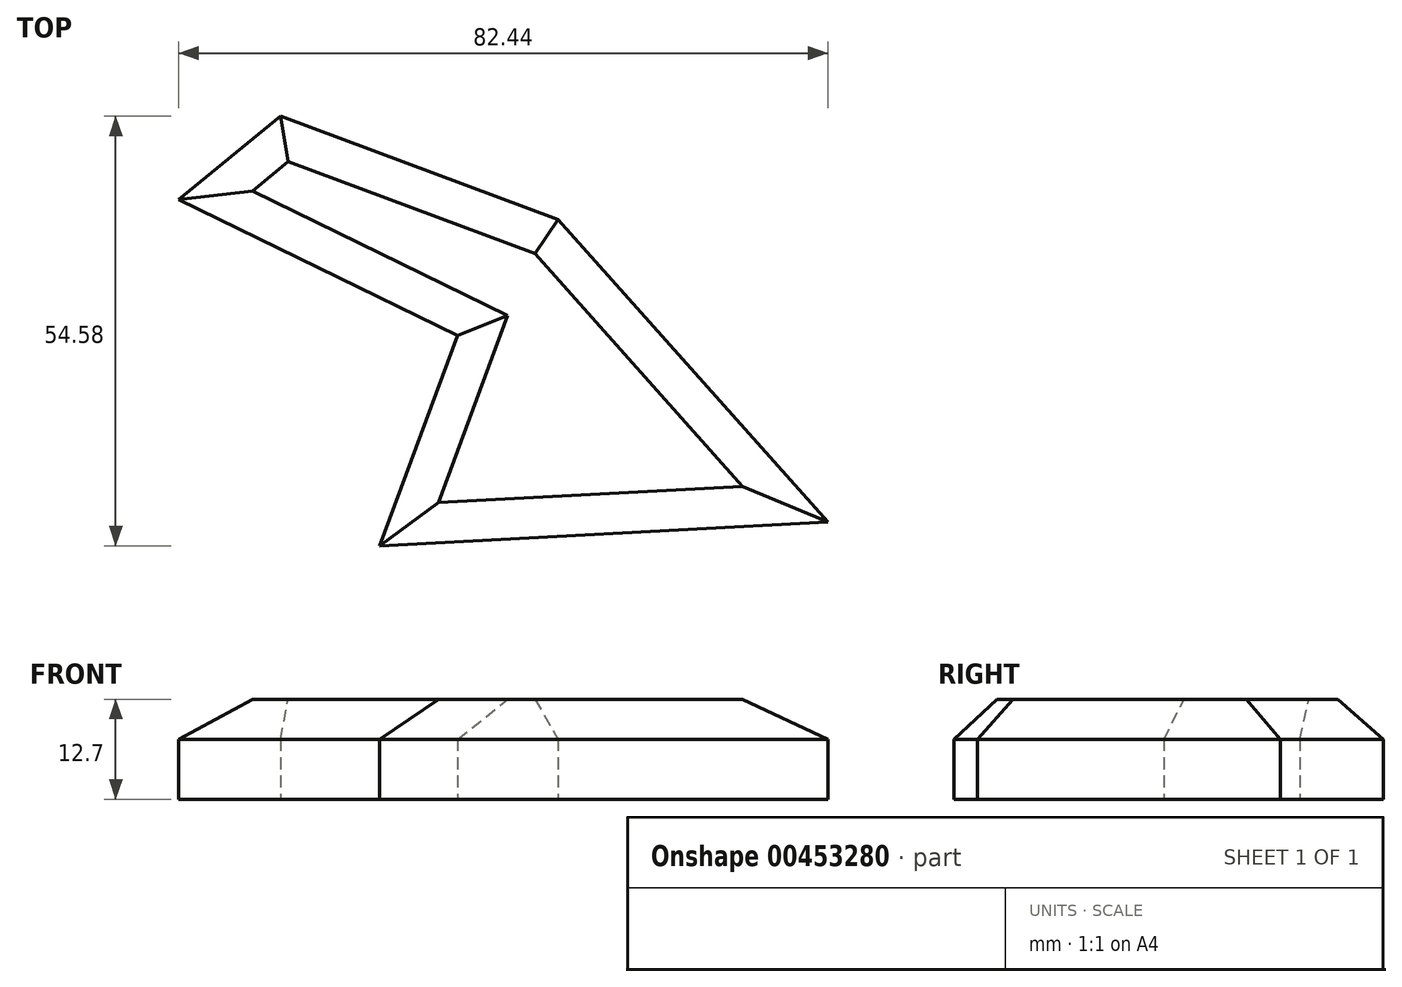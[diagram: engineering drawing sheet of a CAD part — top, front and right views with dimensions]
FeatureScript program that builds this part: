
annotation { "Feature Type Name" : "Feature", "Feature Type Description" : "" }
export const myFeature = defineFeature(function(context is Context, id is Id, definition is map)
    precondition{}
    {
        {
            var Q0;
            Q0=qCreatedBy(makeId("Top.planeOp"),FACE);
            var sketch = newSketch(context, id + "F0", { "sketchPlane" : qUnion([Q0])});
            skLineSegment(sketch, "E0", {"start": v(-43.32, 23.09) * mm, "end": v(-30.4, 33.67) * mm});
            skLineSegment(sketch, "E1", {"start": v(-30.4, 33.67) * mm, "end": v(4.87, 20.57) * mm});
            skLineSegment(sketch, "E2", {"start": v(4.87, 20.57) * mm, "end": v(39.12, -17.88) * mm});
            skLineSegment(sketch, "E3", {"start": v(39.12, -17.88) * mm, "end": v(-17.8, -20.9) * mm});
            skLineSegment(sketch, "E4", {"start": v(-17.8, -20.9) * mm, "end": v(-7.9, 5.8) * mm});
            skLineSegment(sketch, "E5", {"start": v(-7.9, 5.8) * mm, "end": v(-43.32, 23.09) * mm});
            skSolve(sketch);
        }
        {
            var Q0;
            Q0=makeQuery(id+"F0.imprint","IMPRINT",FACE,{"disambiguationData":[TD([[makeQuery(id+"F0.imprint","IMPRINT",EDGE,{"derivedFrom":sQuery(id+"F0.wireOp",EDGE,"E0")}),-1.0]])]});
            extrude(context, id + "F1", {"entities" : qUnion([Q0]), "depth" : 12.7 * mm});
        }
        {
            var Q0;
            Q0=makeQuery(id+"F1.opExtrude","CAP_FACE",FACE,{"disambiguationData":[OSD([sQuery(id+"F0.wireOp",EDGE,"E0"),sQuery(id+"F0.wireOp",EDGE,"E1"),sQuery(id+"F0.wireOp",EDGE,"E2"),sQuery(id+"F0.wireOp",EDGE,"E3"),sQuery(id+"F0.wireOp",EDGE,"E4"),sQuery(id+"F0.wireOp",EDGE,"E5")])],"isStart":false});
            chamfer(context, id + "F2", {"entities" : qUnion([Q0]), "width" : 5.08 * mm, "tangentPropagation" : true});
        }
    });
